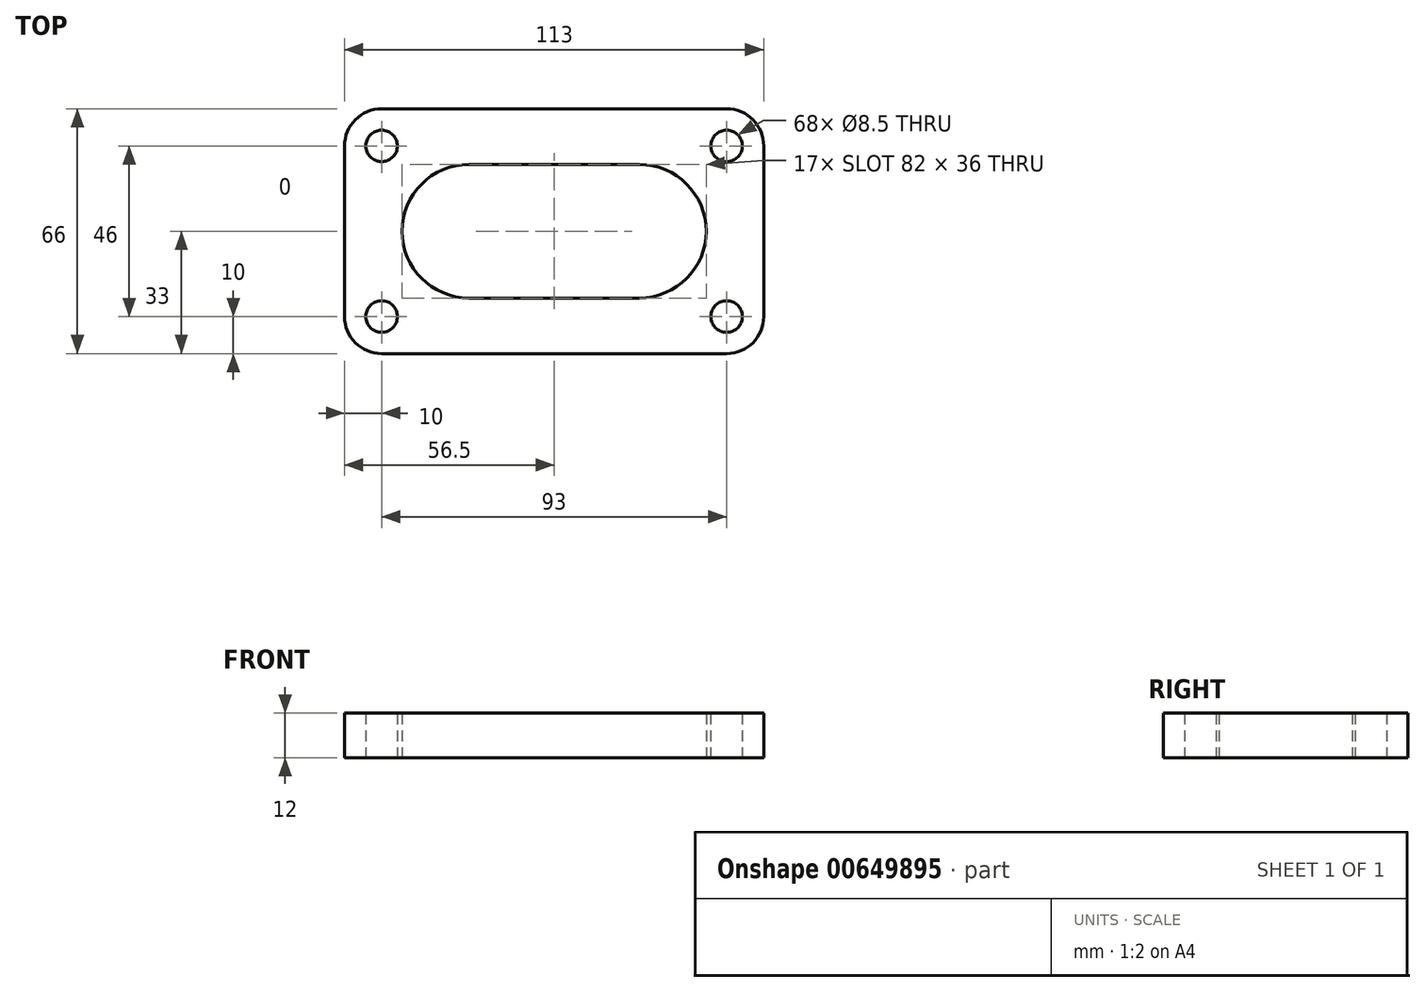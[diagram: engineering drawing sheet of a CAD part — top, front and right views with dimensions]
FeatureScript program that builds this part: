
annotation { "Feature Type Name" : "Feature", "Feature Type Description" : "" }
export const myFeature = defineFeature(function(context is Context, id is Id, definition is map)
    precondition{}
    {
        {
            var Q0;
            Q0=qCreatedBy(makeId("Top.planeOp"),FACE);
            var sketch = newSketch(context, id + "F0", { "sketchPlane" : qUnion([Q0])});
            skCircle(sketch, "E0", {"center": v(-46.5, 23) * mm, "radius": 4.25 * mm});
            skCircle(sketch, "E1", {"center": v(-46.5, -23) * mm, "radius": 4.25 * mm});
            skCircle(sketch, "E2", {"center": v(46.5, 23) * mm, "radius": 4.25 * mm});
            skCircle(sketch, "E3", {"center": v(46.5, -23) * mm, "radius": 4.25 * mm});
            skArc(sketch, "E4", {"start": v(-46.5, 33) * mm, "mid": v(-53.57, 30.07) * mm, "end": v(-56.5, 23) * mm});
            skArc(sketch, "E5", {"start": v(-56.5, -23) * mm, "mid": v(-53.57, -30.07) * mm, "end": v(-46.5, -33) * mm});
            skArc(sketch, "E6", {"start": v(56.5, 23) * mm, "mid": v(53.57, 30.07) * mm, "end": v(46.5, 33) * mm});
            skArc(sketch, "E7", {"start": v(46.5, -33) * mm, "mid": v(53.57, -30.07) * mm, "end": v(56.5, -23) * mm});
            skLineSegment(sketch, "E8", {"start": v(-46.5, 33) * mm, "end": v(46.5, 33) * mm});
            skLineSegment(sketch, "E9", {"start": v(56.5, 23) * mm, "end": v(56.5, -23) * mm});
            skLineSegment(sketch, "E10", {"start": v(-46.5, -33) * mm, "end": v(46.5, -33) * mm});
            skLineSegment(sketch, "E11", {"start": v(-56.5, 23) * mm, "end": v(-56.5, -23) * mm});
            skArc(sketch, "E12.0.startCap", {"start": v(-23, -18) * mm, "mid": v(-41, 0) * mm, "end": v(-23, 18) * mm});
            skArc(sketch, "E12.0.endCap", {"start": v(23, 18) * mm, "mid": v(41, 0) * mm, "end": v(23, -18) * mm});
            skLineSegment(sketch, "E12.0.left", {"start": v(-23, 18) * mm, "end": v(23, 18) * mm});
            skLineSegment(sketch, "E12.0.right", {"start": v(-23, -18) * mm, "end": v(23, -18) * mm});
            skSolve(sketch);
        }
        {
            var Q0;
            Q0=makeQuery(id+"F0.imprint","IMPRINT",FACE,{"disambiguationData":[TD([[makeQuery(id+"F0.imprint","IMPRINT",EDGE,{"derivedFrom":sQuery(id+"F0.wireOp",EDGE,"E0")}),-1.0]])]});
            extrude(context, id + "F1", {"entities" : qUnion([Q0]), "depth" : 12 * mm, "offsetDistance" : 25 * mm});
        }
    });
